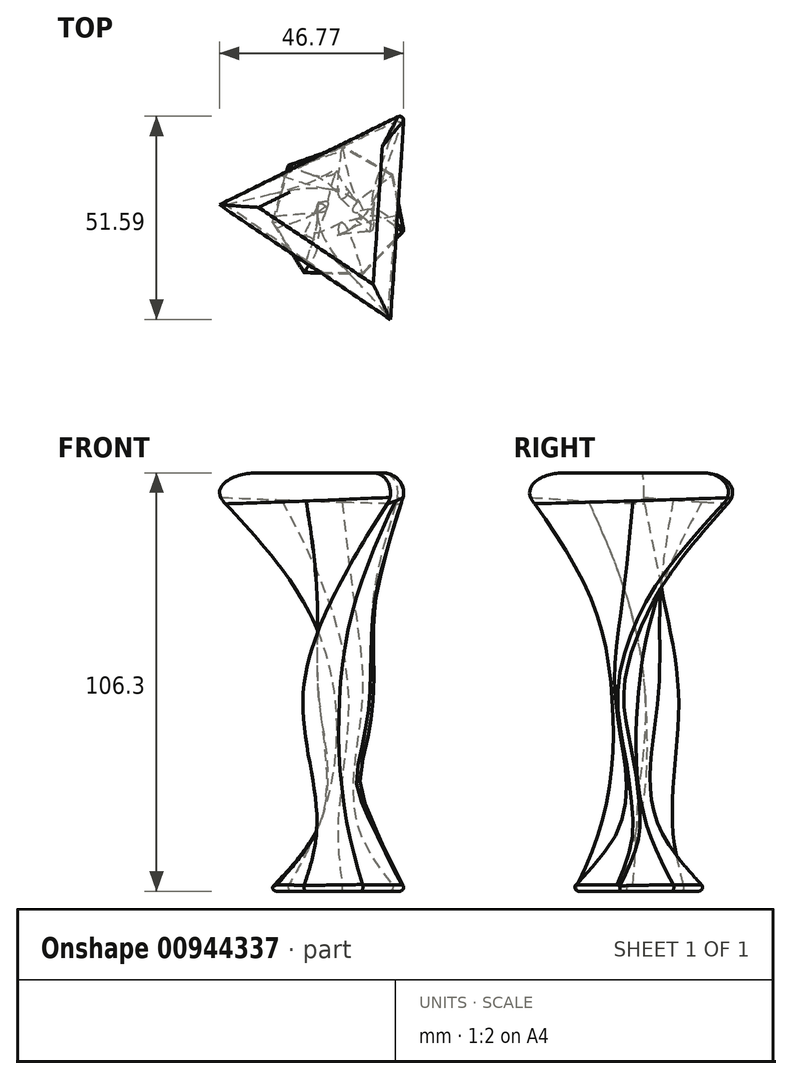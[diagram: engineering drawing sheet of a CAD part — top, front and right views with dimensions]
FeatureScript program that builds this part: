
annotation { "Feature Type Name" : "Feature", "Feature Type Description" : "" }
export const myFeature = defineFeature(function(context is Context, id is Id, definition is map)
    precondition{}
    {
        {
            var Q0;
            Q0=qCreatedBy(makeId("Top.planeOp"),FACE);
            cPlane(context, id + "F0", {"entities" : qUnion([Q0]), "cplaneType" : CPlaneType.OFFSET, "offset" : 34.4 * mm, "width" : 150 * mm, "height" : 150 * mm});
        }
        {
            var Q0;
            Q0=qCreatedBy(makeId("Top.planeOp"),FACE);
            cPlane(context, id + "F1", {"entities" : qUnion([Q0]), "cplaneType" : CPlaneType.OFFSET, "offset" : 90.9 * mm, "width" : 150 * mm, "height" : 150 * mm});
        }
        {
            var Q0;
            Q0=qCreatedBy(makeId("Top.planeOp"),FACE);
            cPlane(context, id + "F2", {"entities" : qUnion([Q0]), "cplaneType" : CPlaneType.OFFSET, "offset" : 56.6 * mm, "width" : 150 * mm, "height" : 150 * mm});
        }
        {
            var Q0;
            Q0=qCreatedBy(makeId("Top.planeOp"),FACE);
            var sketch = newSketch(context, id + "F3", { "sketchPlane" : qUnion([Q0])});
            skCircle(sketch, "E0.cCircle", {"center": v(0, 0) * mm, "radius": 10.77 * mm, "construction": true});
            skLineSegment(sketch, "E0.0", {"start": v(10.77, 0) * mm, "end": v(-5.38, -9.32) * mm});
            skLineSegment(sketch, "E0.1", {"start": v(-5.38, -9.32) * mm, "end": v(-5.38, 9.32) * mm});
            skLineSegment(sketch, "E0.2", {"start": v(-5.38, 9.32) * mm, "end": v(10.77, 0) * mm});
            skSolve(sketch);
        }
        {
            var Q0;
            Q0=qCreatedBy(id+"F0.planeOp",FACE);
            var sketch = newSketch(context, id + "F4", { "sketchPlane" : qUnion([Q0])});
            skCircle(sketch, "E1.cCircle", {"center": v(0, 0) * mm, "radius": 10.8 * mm, "construction": true});
            skLineSegment(sketch, "E1.0", {"start": v(9.78, -4.58) * mm, "end": v(-8.86, -6.18) * mm});
            skLineSegment(sketch, "E1.1", {"start": v(-8.86, -6.18) * mm, "end": v(-0.92, 10.76) * mm});
            skLineSegment(sketch, "E1.2", {"start": v(-0.92, 10.76) * mm, "end": v(9.78, -4.58) * mm});
            skSolve(sketch);
        }
        {
            var Q0;
            Q0=qCreatedBy(id+"F2.planeOp",FACE);
            var sketch = newSketch(context, id + "F5", { "sketchPlane" : qUnion([Q0])});
            skArc(sketch, "E2", {"start": v(10.87, 0) * mm, "mid": v(10.76, 1.58) * mm, "end": v(10.42, 3.12) * mm});
            skCircle(sketch, "E3.cCircle", {"center": v(0, 0) * mm, "radius": 10.87 * mm, "construction": true});
            skLineSegment(sketch, "E3.0", {"start": v(-7.9, 7.46) * mm, "end": v(10.42, 3.12) * mm});
            skLineSegment(sketch, "E3.1", {"start": v(10.42, 3.12) * mm, "end": v(-2.5, -10.58) * mm});
            skLineSegment(sketch, "E3.2", {"start": v(-2.5, -10.58) * mm, "end": v(-7.9, 7.46) * mm});
            skSolve(sketch);
        }
        {
            var Q0;
            Q0=qCreatedBy(id+"F1.planeOp",FACE);
            var sketch = newSketch(context, id + "F6", { "sketchPlane" : qUnion([Q0])});
            skCircle(sketch, "E4.cCircle", {"center": v(0, 0) * mm, "radius": 36.26 * mm, "construction": true});
            skLineSegment(sketch, "E4.0", {"start": v(17.64, -31.68) * mm, "end": v(-36.26, 0.56) * mm});
            skLineSegment(sketch, "E4.1", {"start": v(-36.26, 0.56) * mm, "end": v(18.61, 31.12) * mm});
            skLineSegment(sketch, "E4.2", {"start": v(18.61, 31.12) * mm, "end": v(17.64, -31.68) * mm});
            skSolve(sketch);
        }
        {
            var Q0;
            Q0=qCreatedBy(makeId("Top.planeOp"),FACE);
            cPlane(context, id + "F7", {"entities" : qUnion([Q0]), "cplaneType" : CPlaneType.OFFSET, "offset" : 15.4 * mm, "oppositeDirection" : true, "width" : 150 * mm, "height" : 150 * mm});
        }
        {
            var Q0;
            Q0=qCreatedBy(id+"F7.planeOp",FACE);
            var sketch = newSketch(context, id + "F8", { "sketchPlane" : qUnion([Q0])});
            skCircle(sketch, "E5.cCircle", {"center": v(0, 0) * mm, "radius": 18.2 * mm, "construction": true});
            skLineSegment(sketch, "E5.0", {"start": v(17.41, -5.3) * mm, "end": v(6.7, -16.92) * mm});
            skLineSegment(sketch, "E5.1", {"start": v(6.7, -16.92) * mm, "end": v(-9.05, -15.8) * mm});
            skLineSegment(sketch, "E5.2", {"start": v(-9.05, -15.8) * mm, "end": v(-18, -2.77) * mm});
            skLineSegment(sketch, "E5.3", {"start": v(-18, -2.77) * mm, "end": v(-13.39, 12.34) * mm});
            skLineSegment(sketch, "E5.4", {"start": v(-13.39, 12.34) * mm, "end": v(1.3, 18.16) * mm});
            skLineSegment(sketch, "E5.5", {"start": v(1.3, 18.16) * mm, "end": v(15, 10.3) * mm});
            skLineSegment(sketch, "E5.6", {"start": v(15, 10.3) * mm, "end": v(17.41, -5.3) * mm});
            skSolve(sketch);
        }
        {
            var Q0;
            Q0=makeQuery(id+"F6.imprint","IMPRINT",FACE,{"disambiguationData":[TD([[makeQuery(id+"F6.imprint","IMPRINT",EDGE,{"derivedFrom":sQuery(id+"F6.wireOp",EDGE,"E4.0")}),-1.0]])]});
            var Q1;
            Q1=makeQuery(id+"F5.imprint","IMPRINT",FACE,{"disambiguationData":[TD([[makeQuery(id+"F5.imprint","IMPRINT",EDGE,{"derivedFrom":sQuery(id+"F5.wireOp",EDGE,"E3.0")}),-1.0]])]});
            var Q2;
            Q2=makeQuery(id+"F4.imprint","IMPRINT",FACE,{"disambiguationData":[TD([[makeQuery(id+"F4.imprint","IMPRINT",EDGE,{"derivedFrom":sQuery(id+"F4.wireOp",EDGE,"E1.0")}),-1.0]])]});
            var Q3;
            Q3=makeQuery(id+"F3.imprint","IMPRINT",FACE,{"disambiguationData":[TD([[makeQuery(id+"F3.imprint","IMPRINT",EDGE,{"derivedFrom":sQuery(id+"F3.wireOp",EDGE,"E0.0")}),-1.0]])]});
            var Q4;
            Q4=makeQuery(id+"F8.imprint","IMPRINT",FACE,{"disambiguationData":[TD([[makeQuery(id+"F8.imprint","IMPRINT",EDGE,{"derivedFrom":sQuery(id+"F8.wireOp",EDGE,"E5.0")}),-1.0]])]});
            loft(context, id + "F9", {"sheetProfilesArray" : [{ "sheetProfileEntities" : qUnion([Q0]) }, { "sheetProfileEntities" : qUnion([Q1]) }, { "sheetProfileEntities" : qUnion([Q2]) }, { "sheetProfileEntities" : qUnion([Q3]) }, { "sheetProfileEntities" : qUnion([Q4]) }]});
        }
        {
            var Q0;
            Q0=makeQuery(id+"F9.opLoft","SWEPT_EDGE",EDGE,{"disambiguationData":[OSD([sQuery(id+"F3.wireOp",EDGE,"E0.0"),sQuery(id+"F3.wireOp",EDGE,"E0.2"),sQuery(id+"F4.wireOp",EDGE,"E1.0"),sQuery(id+"F4.wireOp",EDGE,"E1.2"),sQuery(id+"F5.wireOp",EDGE,"E3.0"),sQuery(id+"F5.wireOp",EDGE,"E3.1"),sQuery(id+"F6.wireOp",EDGE,"E4.1"),sQuery(id+"F6.wireOp",EDGE,"E4.2"),sQuery(id+"F8.wireOp",EDGE,"E5.0"),sQuery(id+"F8.wireOp",EDGE,"E5.1")])]});
            fillet(context, id + "F10", {"entities" : qUnion([Q0]), "radius" : 1 * mm, "tangentPropagation" : true, "allowEdgeOverflow" : false});
        }
        {
            var Q0;
            Q0=makeQuery(id+"F9.opLoft","MID_CAP_EDGE",EDGE,{"disambiguationData":[OSD([sQuery(id+"F8.wireOp",EDGE,"E5.3"),sQuery(id+"F8.wireOp",EDGE,"E5.4"),sQuery(id+"F8.wireOp",EDGE,"E5.5")])],"capPos":4.0});
            var Q1;
            Q1=makeQuery(id+"F9.opLoft","MID_CAP_EDGE",EDGE,{"disambiguationData":[OSD([sQuery(id+"F8.wireOp",EDGE,"E5.2"),sQuery(id+"F8.wireOp",EDGE,"E5.3"),sQuery(id+"F8.wireOp",EDGE,"E5.4")])],"capPos":4.0});
            var Q2;
            Q2=makeQuery(id+"F9.opLoft","MID_CAP_EDGE",EDGE,{"disambiguationData":[OSD([sQuery(id+"F8.wireOp",EDGE,"E5.1"),sQuery(id+"F8.wireOp",EDGE,"E5.2"),sQuery(id+"F8.wireOp",EDGE,"E5.3")])],"capPos":4.0});
            var Q3;
            Q3=makeQuery(id+"F9.opLoft","MID_CAP_EDGE",EDGE,{"disambiguationData":[OSD([sQuery(id+"F8.wireOp",EDGE,"E5.0"),sQuery(id+"F8.wireOp",EDGE,"E5.1"),sQuery(id+"F8.wireOp",EDGE,"E5.2")])],"capPos":4.0});
            var Q4;
            Q4=makeQuery(id+"F9.opLoft","MID_CAP_EDGE",EDGE,{"disambiguationData":[OSD([sQuery(id+"F8.wireOp",EDGE,"E5.0"),sQuery(id+"F8.wireOp",EDGE,"E5.5"),sQuery(id+"F8.wireOp",EDGE,"E5.6")])],"capPos":4.0});
            var Q5;
            Q5=makeQuery(id+"F9.opLoft","MID_CAP_EDGE",EDGE,{"disambiguationData":[OSD([sQuery(id+"F8.wireOp",EDGE,"E5.4"),sQuery(id+"F8.wireOp",EDGE,"E5.5"),sQuery(id+"F8.wireOp",EDGE,"E5.6")])],"capPos":4.0});
            var Q6;
            Q6=makeQuery(id+"F9.opLoft","MID_CAP_EDGE",EDGE,{"disambiguationData":[OSD([sQuery(id+"F8.wireOp",EDGE,"E5.0"),sQuery(id+"F8.wireOp",EDGE,"E5.1"),sQuery(id+"F8.wireOp",EDGE,"E5.6")])],"capPos":4.0});
            fillet(context, id + "F11", {"entities" : qUnion([Q0, Q1, Q2, Q3, Q4, Q5, Q6]), "radius" : 1 * mm, "tangentPropagation" : true, "allowEdgeOverflow" : false});
        }
        {
            var Q0;
            Q0=makeQuery(id+"F9.opLoft","MID_CAP_EDGE",EDGE,{"disambiguationData":[OSD([sQuery(id+"F6.wireOp",EDGE,"E4.0"),sQuery(id+"F8.wireOp",EDGE,"E5.3"),sQuery(id+"F8.wireOp",EDGE,"E5.4"),sQuery(id+"F8.wireOp",EDGE,"E5.5")])],"capPos":0.0});
            var Q1;
            Q1=makeQuery(id+"F9.opLoft","MID_CAP_EDGE",EDGE,{"disambiguationData":[OSD([sQuery(id+"F6.wireOp",EDGE,"E4.0"),sQuery(id+"F6.wireOp",EDGE,"E4.1"),sQuery(id+"F8.wireOp",EDGE,"E5.4"),sQuery(id+"F8.wireOp",EDGE,"E5.5")])],"capPos":0.0});
            var Q2;
            Q2=makeQuery(id+"F9.opLoft","MID_CAP_EDGE",EDGE,{"disambiguationData":[OSD([sQuery(id+"F6.wireOp",EDGE,"E4.0"),sQuery(id+"F8.wireOp",EDGE,"E5.2"),sQuery(id+"F8.wireOp",EDGE,"E5.3"),sQuery(id+"F8.wireOp",EDGE,"E5.4")])],"capPos":0.0});
            var Q3;
            Q3=makeQuery(id+"F9.opLoft","MID_CAP_EDGE",EDGE,{"disambiguationData":[OSD([sQuery(id+"F6.wireOp",EDGE,"E4.0"),sQuery(id+"F8.wireOp",EDGE,"E5.1"),sQuery(id+"F8.wireOp",EDGE,"E5.2"),sQuery(id+"F8.wireOp",EDGE,"E5.3")])],"capPos":0.0});
            var Q4;
            Q4=makeQuery(id+"F9.opLoft","MID_CAP_EDGE",EDGE,{"disambiguationData":[OSD([sQuery(id+"F6.wireOp",EDGE,"E4.0"),sQuery(id+"F6.wireOp",EDGE,"E4.2"),sQuery(id+"F8.wireOp",EDGE,"E5.1"),sQuery(id+"F8.wireOp",EDGE,"E5.2")])],"capPos":0.0});
            var Q5;
            {var subQ0=sQuery(id+"F6.wireOp",EDGE,"E4.2");var subQ1=sQuery(id+"F6.wireOp",EDGE,"E4.1");var subQ2=sQuery(id+"F6.wireOp",EDGE,"E4.0");Q5=makeQuery(id+"F9.opLoft","MID_CAP_EDGE",EDGE,{"disambiguationData":[OSD([subQ2,subQ1,subQ0]),TDD([makeQuery(id+"F6.imprint","INTERSECT",VERTEX,{"derivedFrom":[subQ2,subQ0]}),makeQuery(id+"F6.imprint","INTERSECT",VERTEX,{"derivedFrom":[subQ1,subQ0]}),makeQuery(id+"F6.imprint","IMPRINT",EDGE,{"derivedFrom":subQ0})])],"capPos":0.0});}
            var Q6;
            {var subQ0=sQuery(id+"F6.wireOp",EDGE,"E4.1");var subQ1=sQuery(id+"F6.wireOp",EDGE,"E4.2");var subQ2=sQuery(id+"F6.wireOp",EDGE,"E4.0");Q6=makeQuery(id+"F9.opLoft","MID_CAP_EDGE",EDGE,{"disambiguationData":[OSD([subQ2,subQ0,subQ1]),TDD([makeQuery(id+"F6.imprint","INTERSECT",VERTEX,{"derivedFrom":[subQ2,subQ0]}),makeQuery(id+"F6.imprint","INTERSECT",VERTEX,{"derivedFrom":[subQ0,subQ1]}),makeQuery(id+"F6.imprint","IMPRINT",EDGE,{"derivedFrom":subQ0})])],"capPos":0.0});}
            fillet(context, id + "F12", {"entities" : qUnion([Q0, Q1, Q2, Q3, Q4, Q5, Q6]), "radius" : 5 * mm, "tangentPropagation" : true, "allowEdgeOverflow" : false});
        }
        {
            var Q0;
            Q0=makeQuery(id+"F9.opLoft","SWEPT_EDGE",EDGE,{"disambiguationData":[OSD([sQuery(id+"F3.wireOp",EDGE,"E0.1"),sQuery(id+"F4.wireOp",EDGE,"E1.1"),sQuery(id+"F5.wireOp",EDGE,"E3.2"),sQuery(id+"F6.wireOp",EDGE,"E4.0"),sQuery(id+"F8.wireOp",EDGE,"E5.1"),sQuery(id+"F8.wireOp",EDGE,"E5.2"),sQuery(id+"F8.wireOp",EDGE,"E5.3")])]});
            fillet(context, id + "F13", {"entities" : qUnion([Q0]), "radius" : 5 * mm, "tangentPropagation" : true, "allowEdgeOverflow" : false});
        }
    });
